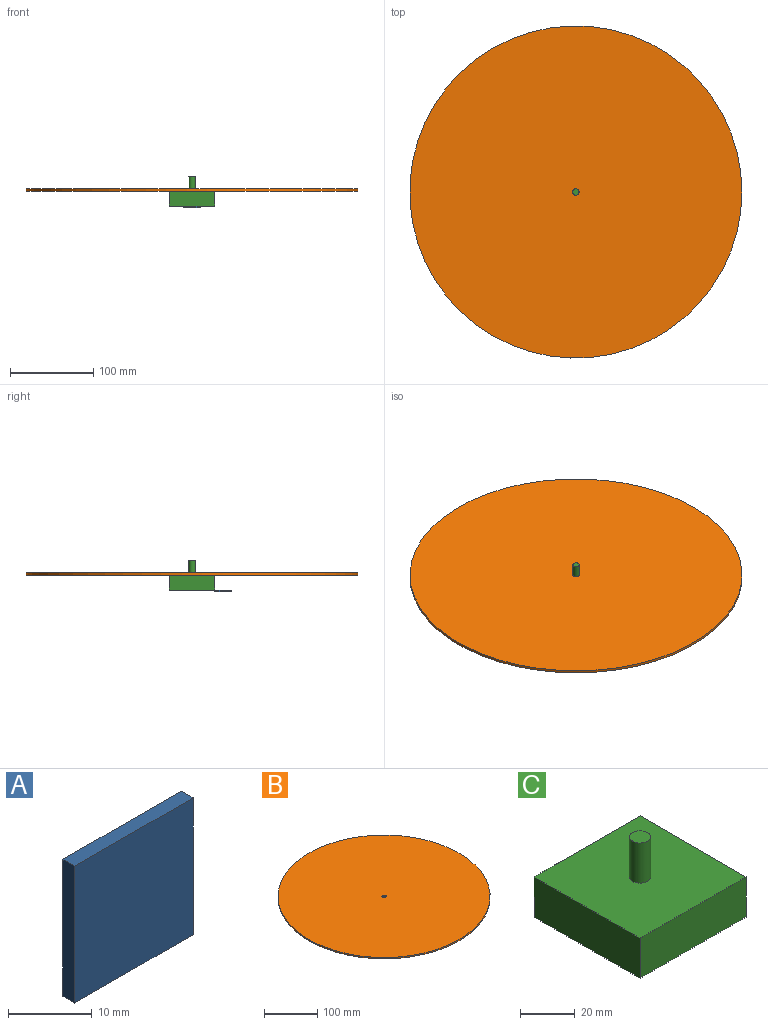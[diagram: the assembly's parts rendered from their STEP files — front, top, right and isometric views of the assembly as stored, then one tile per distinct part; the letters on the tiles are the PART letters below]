
ASSEMBLY  parts=3 mates=3
PART A: 6 faces, bbox 20x2x20 mm
  f0: plane 20x2mm, normal (0,0,-1), area 40mm2, adj f1,f3,f4,f5
  f1: plane 20x2mm, normal (1,0,0), area 40mm2, adj f0,f2,f4,f5
  f2: plane 20x2mm, normal (0,0,1), area 40mm2, adj f1,f3,f4,f5
  f3: plane 20x2mm, normal (-1,0,0), area 40mm2, adj f0,f2,f4,f5
  f4: plane 20x20mm, normal (0,-1,0), area 400mm2, adj f0,f1,f2,f3
  f5: plane 20x20mm, normal (0,1,0), area 400mm2, adj f0,f1,f2,f3
PART B: 4 faces, bbox 400x400x3 mm
  f0: cylinder r=3.9mm len=7.8mm, axis (0,0,-1), area 73.5mm2, adj f2,f3
  f1: cylinder r=200mm len=400mm, axis (0,0,-1), area 3769.9mm2, adj f2,f3
  f2: plane 400x400mm, normal (0,0,1), area 125615.9mm2, adj f0,f1
  f3: plane 400x400mm, normal (0,0,-1), area 125615.9mm2, adj f0,f1
PART C: 8 faces, bbox 55x55x36 mm
  f0: plane 55x18mm, normal (-1,0,0), area 990mm2, adj f1,f3,f4,f5
  f1: plane 55x18mm, normal (0,-1,0), area 990mm2, adj f0,f2,f4,f5
  f2: plane 55x18mm, normal (1,0,0), area 990mm2, adj f1,f3,f4,f5
  f3: plane 55x18mm, normal (0,1,0), area 990mm2, adj f0,f2,f4,f5
  f4: plane 55x55mm, normal (0,0,1), area 2977.2mm2, adj f0,f1,f2,f3,f6
  f5: plane 55x55mm, normal (0,0,-1), area 3025mm2, adj f0,f1,f2,f3
  f6: cylinder r=3.9mm len=18mm, axis (0,0,-1), area 441.1mm2, adj f4,f7
  f7: plane 7.8x7.8mm, normal (0,0,1), area 47.8mm2, adj f6
PLACE A rot(axis=(1,0,0),90deg) t=(182.37,-32.81,-69.81)mm
PLACE B t=(172.37,-5.31,-51.81)mm
PLACE C t=(144.87,-32.81,-69.81)mm
MATE fastened C.f6 <-> B.f0  axis (0,0,1) through (172.37,-5.31,-51.81)mm
MATE cylindrical C.f6 <-> B.f0  axis (0,0,-1) through (172.37,-5.31,-42.81)mm
MATE fastened A.f5 <-> C.f5  axis (0,0,1) through (172.37,-32.81,-69.81)mm
